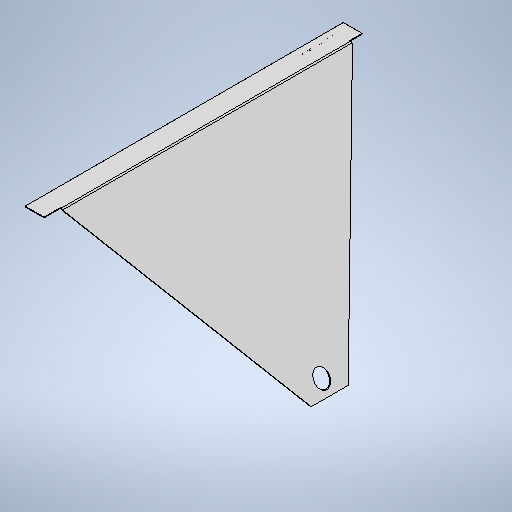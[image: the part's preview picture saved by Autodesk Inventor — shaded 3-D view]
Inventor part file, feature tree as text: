
AUTODESK INVENTOR PART (.ipt)
format: ipt  version: 2025 (Build 290162010, 162A)  size: 375,296 bytes
history: native  units: mm
features: sketch x5, sheet_metal_op x3, extrude x3, other x2, projected_geometry x1
ambient origin geometry x8: Origin, YZ Plane, XZ Plane, XY Plane, X Axis, Y Axis, Z Axis, Center Point
bodies: Body1 (feature_tree)
feature tree (14):
  sheet_metal_op  "Contour Flange2"
  extrude  "Extrusion7"  Depth=88.0mm
  extrude  "Extrusion11"  Depth=230.0mm
  extrude  "Extrusion14"  Depth=4.0mm
  other  "Mark2"
  sketch  "Sketch1"  dims[d0=1150.0mm d61=88.0mm]
  other  "Plate4"
  sheet_metal_op  "Bend4"
  sheet_metal_op  "Corner4"
  sketch  "Sketch10"  dims[d63=10.0mm d64=230.0mm]
  sketch  "Sketch14"  dims[d65=800.0mm d66=4.0mm]
  sketch  "Sketch17"  dims[d67=4.0mm]
  projected_geometry  "Projected Loop11"
  sketch  "Sketch19"  dims[d68=2.0mm d69=8.0mm d70=6.0mm d71=1536.0mm d72=6.0mm d73=4.0mm d74=16.0mm d75=4.0mm d76=6.0mm d81=10.0mm d82=0.0mm d86=60.0mm d99=76.5mm d100=0.0mm d101=0.0mm d102=60.0mm d103=50.0mm d110=3.0mm d111=196.0mm d112=66.0mm d113=100.0mm d114=87.0mm d115=100.0mm d116=4.0mm d117=0.0mm]
